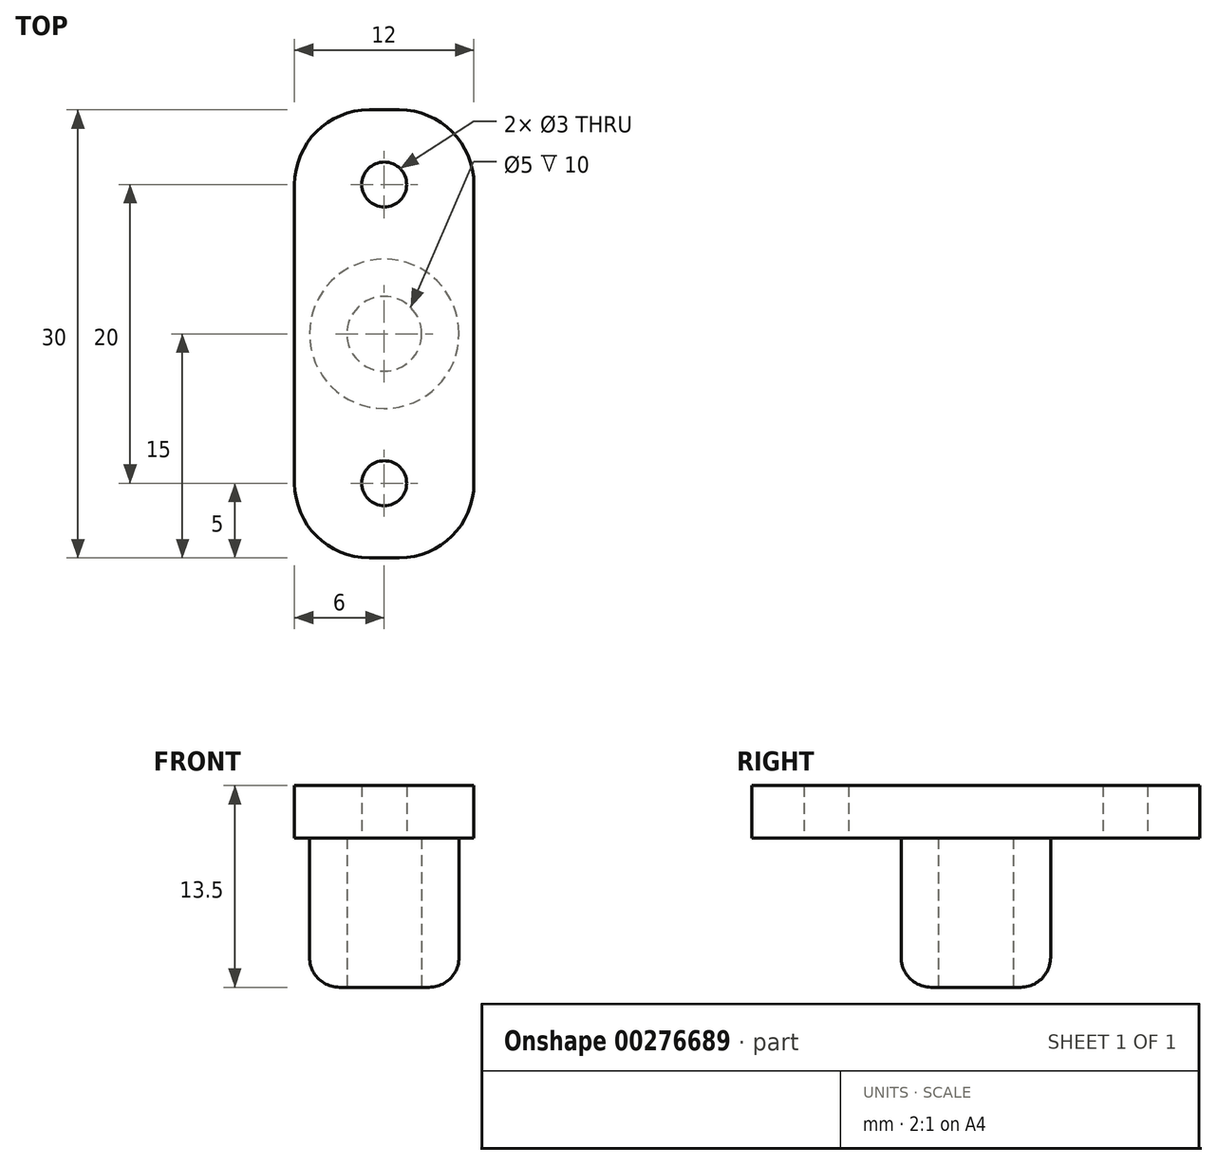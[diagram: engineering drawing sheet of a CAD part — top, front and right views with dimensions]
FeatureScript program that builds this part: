
annotation { "Feature Type Name" : "Feature", "Feature Type Description" : "" }
export const myFeature = defineFeature(function(context is Context, id is Id, definition is map)
    precondition{}
    {
        {
            var Q0;
            Q0=qCreatedBy(makeId("Top.planeOp"),FACE);
            var sketch = newSketch(context, id + "F0", { "sketchPlane" : qUnion([Q0])});
            skCircle(sketch, "E0", {"center": v(0, 0) * mm, "radius": 2.5 * mm});
            skCircle(sketch, "E1", {"center": v(0, 0) * mm, "radius": 5 * mm});
            skSolve(sketch);
        }
        {
            var Q0;
            Q0 = qSketchRegion(id + "F0", true);
            extrude(context, id + "F1", {"entities" : qUnion([Q0]), "depth" : 10 * mm});
        }
        {
            var Q0;
            Q0=makeQuery(id+"F1.opExtrude","CAP_FACE",FACE,{"disambiguationData":[OSD([sQuery(id+"F0.wireOp",EDGE,"E0"),sQuery(id+"F0.wireOp",EDGE,"E1")])],"isStart":false});
            var sketch = newSketch(context, id + "F2", { "sketchPlane" : qUnion([Q0])});
            skLineSegment(sketch, "E2.bottom", {"start": v(-6, 15) * mm, "end": v(6, 15) * mm});
            skLineSegment(sketch, "E2.top", {"start": v(-6, -15) * mm, "end": v(6, -15) * mm});
            skLineSegment(sketch, "E2.left", {"start": v(-6, 15) * mm, "end": v(-6, -15) * mm});
            skLineSegment(sketch, "E2.right", {"start": v(6, 15) * mm, "end": v(6, -15) * mm});
            skCircle(sketch, "E3", {"center": v(0, 10) * mm, "radius": 1.5 * mm});
            skCircle(sketch, "E4", {"center": v(0, -10) * mm, "radius": 1.5 * mm});
            skSolve(sketch);
        }
        {
            var Q0;
            Q0 = qSketchRegion(id + "F2", true);
            extrude(context, id + "F3", {"entities" : qUnion([Q0]), "operationType" : NewBodyOperationType.ADD, "depth" : 3.5 * mm});
        }
        {
            var Q0;
            Q0=makeQuery(id+"F3.opExtrude","SWEPT_EDGE",EDGE,{"disambiguationData":[OSD([sQuery(id+"F2.wireOp",EDGE,"E2.bottom"),sQuery(id+"F2.wireOp",EDGE,"E2.right")])]});
            var Q1;
            Q1=makeQuery(id+"F3.opExtrude","SWEPT_EDGE",EDGE,{"disambiguationData":[OSD([sQuery(id+"F2.wireOp",EDGE,"E2.bottom"),sQuery(id+"F2.wireOp",EDGE,"E2.left")])]});
            var Q2;
            Q2=makeQuery(id+"F3.opExtrude","SWEPT_EDGE",EDGE,{"disambiguationData":[OSD([sQuery(id+"F2.wireOp",EDGE,"E2.top"),sQuery(id+"F2.wireOp",EDGE,"E2.left")])]});
            var Q3;
            Q3=makeQuery(id+"F3.opExtrude","SWEPT_EDGE",EDGE,{"disambiguationData":[OSD([sQuery(id+"F2.wireOp",EDGE,"E2.top"),sQuery(id+"F2.wireOp",EDGE,"E2.right")])]});
            fillet(context, id + "F4", {"entities" : qUnion([Q0, Q1, Q2, Q3]), "radius" : 5 * mm, "tangentPropagation" : true, "allowEdgeOverflow" : false});
        }
        {
            var Q0;
            Q0=makeQuery(id+"F1.opExtrude","CAP_EDGE",EDGE,{"disambiguationData":[OSD([sQuery(id+"F0.wireOp",EDGE,"E1")])],"isStart":true});
            fillet(context, id + "F5", {"entities" : qUnion([Q0]), "radius" : 2 * mm, "tangentPropagation" : true, "allowEdgeOverflow" : false});
        }
    });
